# Revit family: equip-sink-undr-elkay-double-lustertone
name_source: partatom
category: Plumbing Fixtures
units: mm (PartAtom-declared; Revit-internal decimal feet)

## family parameters
Always vertical = Yes
Cut with Voids When Loaded = No
OmniClass Number = 23.45.05.14.14.27
OmniClass Title = Service Sinks
Part Type = Normal
Room Calculation Point = No
Round Connector Dimension = Use Radius
Shared = No
Work Plane-Based = No

## types (1)
- ByType
    Assembly Code = D2010410
    Bowl Length = 1' - 1 1/2"
    Bowl Width = 1' - 4"
    CL Sink to CL Partition = 0' - 0"
    CL Sink to CL Partition Hidden = 0' - 0"
    Custom Bowl = No
    Custom Bowl Length = 1' - 1 1/2"
    Description = Lustertone Double Bowl Sink
    Drain Location = 0' - 5"
    Left Bowl Length = 1' - 1 1/2"
    Manufacturer = Elkay Manufacturing
    MasterFormat Number = 22.42.16.16
    MasterFormat Title = Commercial Sinks
    Model = Lustertone Undermount
    Nominal Dia = 0' - 1 1/2"
    Nominal Radius = 0' - 0 3/4"
    OmniClass Code = 23.45.05.14.14.27
    OmniClass Title = Service Sinks
    Partition Width = 0' - 1 1/4"
    Sanitary Flow Rate = 10 GPM
    Sink Bowl Formula = 1' - 1 1/2"
    Sink Depth = 0' - 7 7/8"
    Sink Ledge Back Width = 0' - 1 1/4"
    Sink Ledge Front Width = 0' - 1 1/4"
    Sink Ledge Sides Width = 0' - 1 1/4"
    Sink Length = 2' - 6 3/4"
    Sink Material = Metal - Steel - Stainless - Chrome
    Sink Width = 1' - 6 1/2"
    URL = www.elkayusa.com

## geometry (parser evidence)
native form markers: Sweep x4
no freeform markers — native parametric forms only
